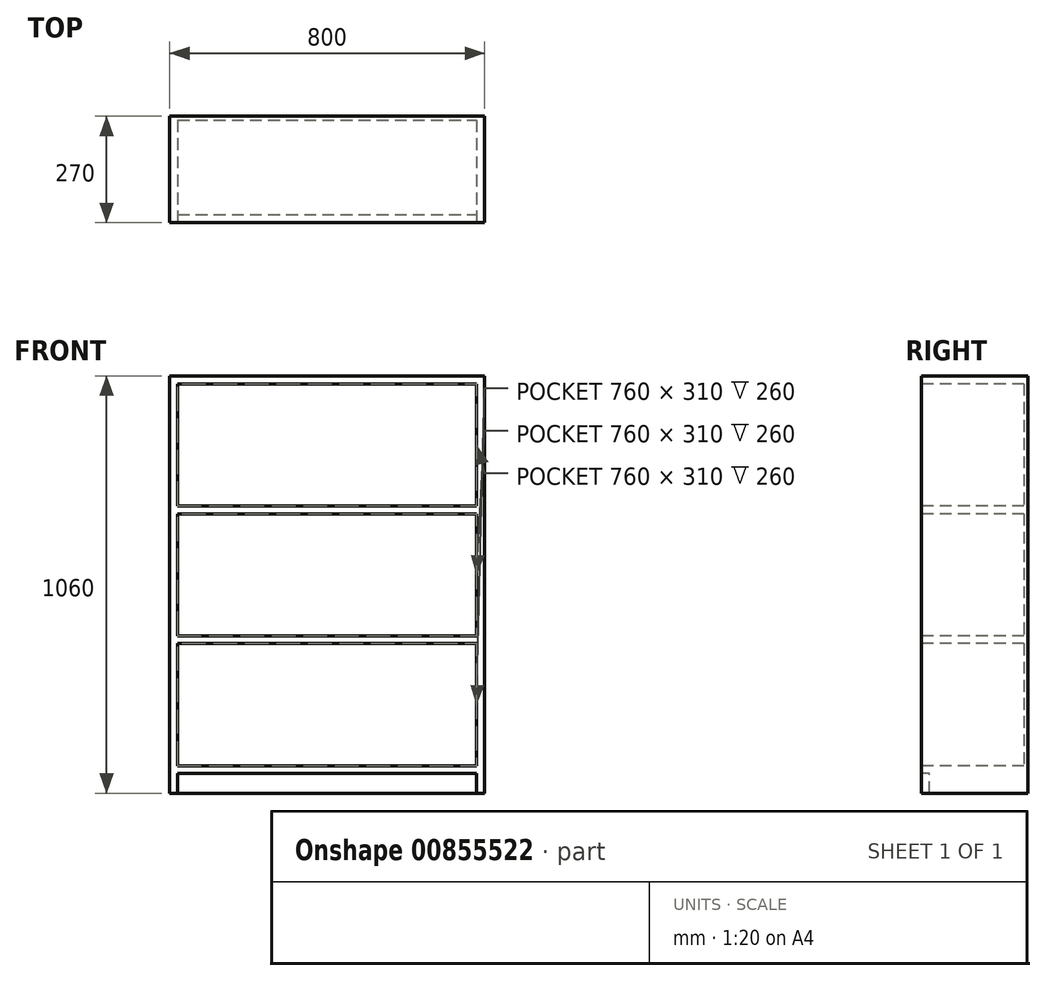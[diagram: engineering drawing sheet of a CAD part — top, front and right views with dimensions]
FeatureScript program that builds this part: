
annotation { "Feature Type Name" : "Feature", "Feature Type Description" : "" }
export const myFeature = defineFeature(function(context is Context, id is Id, definition is map)
    precondition{}
    {
        {
            var Q0;
            Q0=qCreatedBy(makeId("Top.planeOp"),FACE);
            var sketch = newSketch(context, id + "F0", { "sketchPlane" : qUnion([Q0])});
            skLineSegment(sketch, "E0.bottom", {"start": v(-256.84, 119.6) * mm, "end": v(543.16, 119.6) * mm});
            skLineSegment(sketch, "E0.top", {"start": v(-256.84, -150.4) * mm, "end": v(543.16, -150.4) * mm});
            skLineSegment(sketch, "E0.left", {"start": v(-256.84, 119.6) * mm, "end": v(-256.84, -150.4) * mm});
            skLineSegment(sketch, "E0.right", {"start": v(543.16, 119.6) * mm, "end": v(543.16, -150.4) * mm});
            skSolve(sketch);
        }
        {
            var Q0;
            Q0=makeQuery(id+"F0.imprint","IMPRINT",FACE,{"disambiguationData":[TD([[makeQuery(id+"F0.imprint","IMPRINT",EDGE,{"derivedFrom":sQuery(id+"F0.wireOp",EDGE,"E0.bottom")}),-1.0]])]});
            extrude(context, id + "F1", {"entities" : qUnion([Q0]), "depth" : 1060 * mm, "offsetDistance" : 25.4 * mm});
        }
        {
            var Q0;
            Q0=makeQuery(id+"F1.opExtrude","SWEPT_FACE",FACE,{"disambiguationData":[OSD([sQuery(id+"F0.wireOp",EDGE,"E0.top")])]});
            var sketch = newSketch(context, id + "F2", { "sketchPlane" : qUnion([Q0])});
            skLineSegment(sketch, "E1.bottom", {"start": v(-236.84, 0) * mm, "end": v(523.16, 0) * mm});
            skLineSegment(sketch, "E1.top", {"start": v(-236.84, 50) * mm, "end": v(523.16, 50) * mm});
            skLineSegment(sketch, "E1.left", {"start": v(-236.84, 0) * mm, "end": v(-236.84, 50) * mm});
            skLineSegment(sketch, "E1.right", {"start": v(523.16, 0) * mm, "end": v(523.16, 50) * mm});
            skSolve(sketch);
        }
        {
            var Q0;
            Q0=makeQuery(id+"F2.imprint","IMPRINT",FACE,{"disambiguationData":[TD([[makeQuery(id+"F2.imprint","IMPRINT",EDGE,{"derivedFrom":sQuery(id+"F2.wireOp",EDGE,"E1.bottom")}),1.0]])]});
            extrude(context, id + "F3", {"entities" : qUnion([Q0]), "operationType" : NewBodyOperationType.REMOVE, "oppositeDirection" : true, "depth" : 20 * mm, "offsetDistance" : 25.4 * mm});
        }
        {
            var Q0;
            Q0=makeQuery(id+"F1.opExtrude","SWEPT_FACE",FACE,{"disambiguationData":[OSD([sQuery(id+"F0.wireOp",EDGE,"E0.top")])]});
            var sketch = newSketch(context, id + "F4", { "sketchPlane" : qUnion([Q0])});
            skLineSegment(sketch, "E2.bottom", {"start": v(-236.84, 1040) * mm, "end": v(523.16, 1040) * mm});
            skLineSegment(sketch, "E2.top", {"start": v(-236.84, 730) * mm, "end": v(523.16, 730) * mm});
            skLineSegment(sketch, "E2.left", {"start": v(-236.84, 1040) * mm, "end": v(-236.84, 730) * mm});
            skLineSegment(sketch, "E2.right", {"start": v(523.16, 1040) * mm, "end": v(523.16, 730) * mm});
            skLineSegment(sketch, "E3.0.1.0", {"start": v(523.16, 710) * mm, "end": v(523.16, 400) * mm});
            skLineSegment(sketch, "E3.0.1.1", {"start": v(-236.84, 710) * mm, "end": v(-236.84, 400) * mm});
            skLineSegment(sketch, "E3.0.1.2", {"start": v(-236.84, 400) * mm, "end": v(523.16, 400) * mm});
            skLineSegment(sketch, "E3.0.1.3", {"start": v(-236.84, 710) * mm, "end": v(523.16, 710) * mm});
            skLineSegment(sketch, "E3.0.2.0", {"start": v(523.16, 380) * mm, "end": v(523.16, 70) * mm});
            skLineSegment(sketch, "E3.0.2.1", {"start": v(-236.84, 380) * mm, "end": v(-236.84, 70) * mm});
            skLineSegment(sketch, "E3.0.2.2", {"start": v(-236.84, 70) * mm, "end": v(523.16, 70) * mm});
            skLineSegment(sketch, "E3.0.2.3", {"start": v(-236.84, 380) * mm, "end": v(523.16, 380) * mm});
            skLineSegment(sketch, "E3.direction1", {"start": v(-236.84, 730) * mm, "end": v(-211.44, 730) * mm, "construction": true});
            skLineSegment(sketch, "E3.direction2", {"start": v(-236.84, 730) * mm, "end": v(-236.84, 400) * mm, "construction": true});
            skSolve(sketch);
        }
        {
            var Q0;
            Q0=makeQuery(id+"F4.imprint","IMPRINT",FACE,{"disambiguationData":[TD([[makeQuery(id+"F4.imprint","IMPRINT",EDGE,{"derivedFrom":sQuery(id+"F4.wireOp",EDGE,"E2.bottom")}),-1.0]])]});
            var Q1;
            Q1=makeQuery(id+"F4.imprint","IMPRINT",FACE,{"disambiguationData":[TD([[makeQuery(id+"F4.imprint","IMPRINT",EDGE,{"derivedFrom":sQuery(id+"F4.wireOp",EDGE,"E3.0.1.0")}),-1.0]])]});
            var Q2;
            Q2=makeQuery(id+"F4.imprint","IMPRINT",FACE,{"disambiguationData":[TD([[makeQuery(id+"F4.imprint","IMPRINT",EDGE,{"derivedFrom":sQuery(id+"F4.wireOp",EDGE,"E3.0.2.0")}),-1.0]])]});
            extrude(context, id + "F5", {"entities" : qUnion([Q0, Q1, Q2]), "operationType" : NewBodyOperationType.REMOVE, "oppositeDirection" : true, "depth" : 260 * mm, "offsetDistance" : 25.4 * mm});
        }
    });
